# Revit family: HYDRO UNIT
name_source: partatom
category: Mechanical Equipment
revit_build: Autodesk Revit 2015 (Build: 20140606_1530(x64)
units: mm (PartAtom-declared; Revit-internal decimal feet)

## types (24) — shared parameters
Clearance Offset Back = 0.000 mm
Manufacturer = SAMSUNG
URL = www.samsung.com

## per-type parameters (varying)
| type | Model | Voltage |
| 4.40 kW, 220-240V, HYDRO UNIT(1) | AE090MNYDEH/EU | 220-240V |
| 6.60 kW, 220-240V, HYDRO UNIT | AE090MNYDEH/EU | 220-240V |
| 9.00 kW, 220-240V, HYDRO UNIT(1) | AE090MNYDGH/EU | 220-240V |
| 9.00 kW, 380-415V, HYDRO UNIT(1) | AE090MNYDGH/EU | 380-415V |
| 12.00 kW, 220-240V, HYDRO UNIT(1) | AE160MNYDEH/EU | 220-240V |
| 14.50 kW, 220-240V, HYDRO UNIT | AE160MNYDEH/EU | 220-240V |
| 12.00 kW, 380-415V, HYDRO UNIT(1) | AE160MNYDGH/EU | 380-415V |
| 14.50 kW, 380-415V, HYDRO UNIT | AE160MNYDGH/EU | 380-415V |
| 6.00 kW, 220-240V, HYDRO UNIT(1) | NH080PHXEA | 220-240V |
| 7.00 kW, 220-240V, HYDRO UNIT | NH080PHXEA | 220-240V |
| 8.00 kW, 220-240V, HYDRO UNIT | NH080PHXEA | 220-240V |
| 11.00 kW, 220-240V, HYDRO UNIT | NH160PHXEA | 220-240V |
| 14.00 kW, 220-240V, HYDRO UNIT(1) | NH160PHXEA | 220-240V |
| 16.00 kW, 220-240V, HYDRO UNIT(1) | NH160PHXEA | 220-240V |
| 4.40 kW, 220-240V, HYDRO UNIT(2) | AE090JNYDEH/EU | 220-240V |
| 6.00 kW, 220-240V, HYDRO UNIT(2) | AE090JNYDEH/EU | 220-240V |
| 9.00 kW, 220-240V, HYDRO UNIT(2) | AE090JNYDEH/EU | 220-240V |
| 12.00 kW, 220-240V, HYDRO UNIT(2) | AE160JNYDEH/EU | 220~240V |
| 14.00 kW, 220-240V, HYDRO UNIT(2) | AE160JNYDEH/EU | 220-240V |
| 16.00 kW, 220-240V, HYDRO UNIT(2) | AE160JNYDEH/EU | 220-240V |
| 9.00 kW, 380-415V, HYDRO UNIT(2) | AE090JNYDGH/EU | 380-415V |
| 12.00 kW, 380-415V, HYDRO UNIT(2) | AE160JNYDGH/EU | 220-240V |
| 14.00 kW, 380-415V, HYDRO UNIT | AE160JNYDGH/EU | 220-240V |
| 16.00 kW, 380-415V, HYDRO UNIT | AE160JNYDGH/EU | 220-240V |

## geometry (parser evidence)
native form markers: Sweep x2
no freeform markers — native parametric forms only
